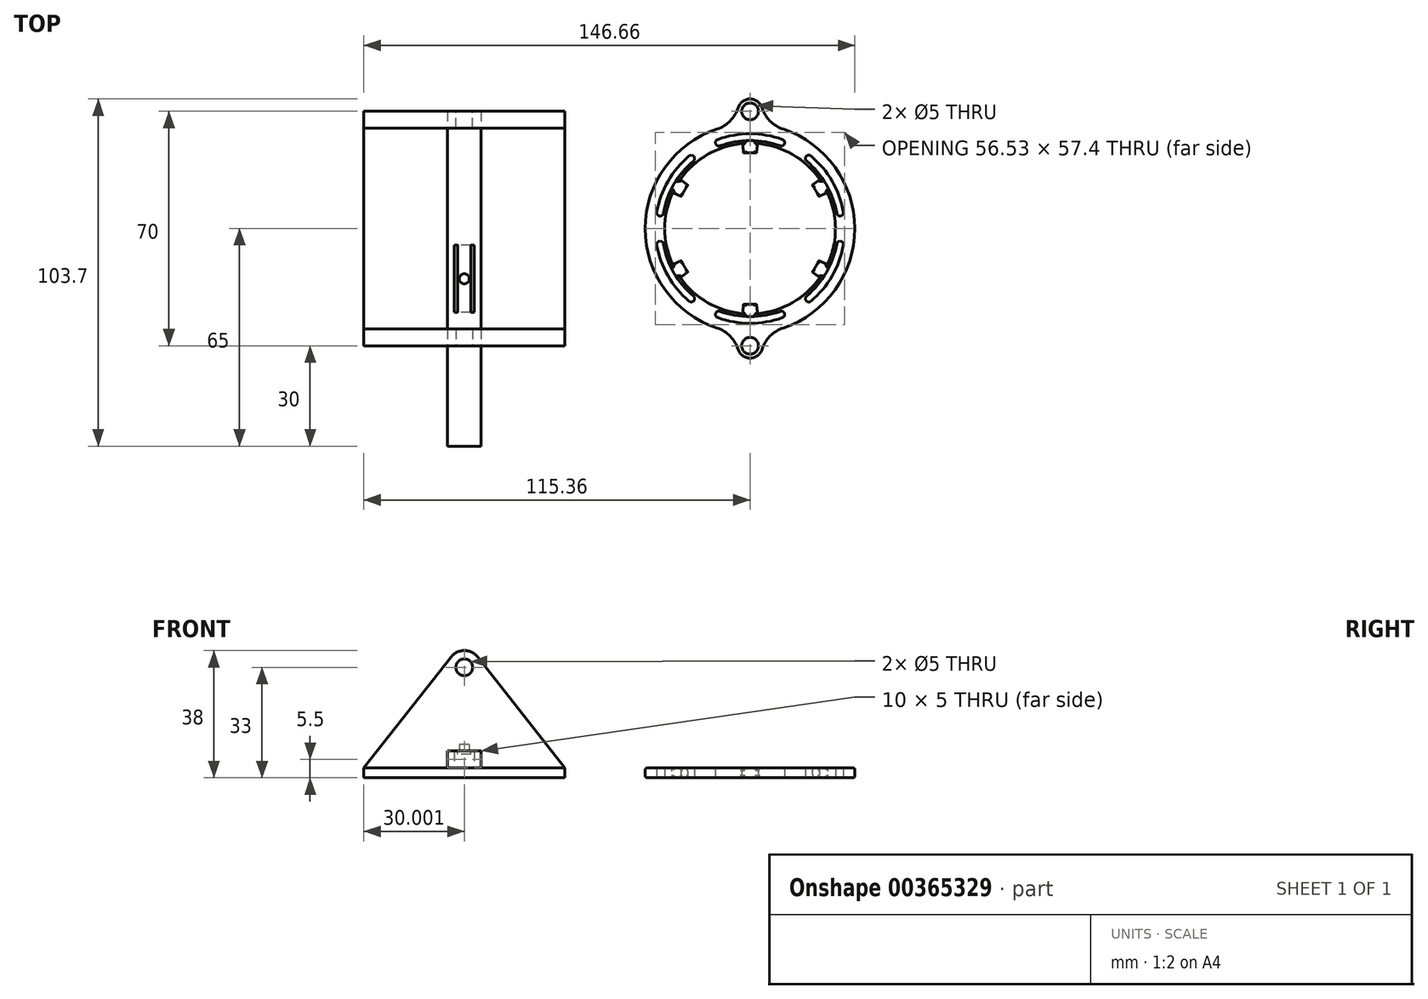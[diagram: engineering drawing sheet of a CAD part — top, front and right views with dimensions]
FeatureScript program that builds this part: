
annotation { "Feature Type Name" : "Feature", "Feature Type Description" : "" }
export const myFeature = defineFeature(function(context is Context, id is Id, definition is map)
    precondition{}
    {
        {
            var Q0;
            Q0=qCreatedBy(makeId("Top.planeOp"),FACE);
            var sketch = newSketch(context, id + "F0", { "sketchPlane" : qUnion([Q0])});
            skArc(sketch, "E0", {"start": v(-2.22, 25.4) * mm, "mid": v(-12.75, 22.08) * mm, "end": v(-20.89, 14.63) * mm});
            skArc(sketch, "E1", {"start": v(-9.89, 29.7) * mm, "mid": v(-31.3, 0) * mm, "end": v(-9.89, -29.7) * mm});
            skArc(sketch, "E2", {"start": v(1.97, 22.56) * mm, "mid": v(0, 22.65) * mm, "end": v(-1.97, 22.56) * mm});
            skArc(sketch, "E3", {"start": v(9, 24.71) * mm, "mid": v(0, 26.3) * mm, "end": v(-9, 24.71) * mm});
            skArc(sketch, "E4", {"start": v(9.68, 26.6) * mm, "mid": v(0, 28.3) * mm, "end": v(-9.68, 26.6) * mm});
            skLineSegment(sketch, "E5", {"start": v(0, 0) * mm, "end": v(-1.97, 22.56) * mm, "construction": true});
            skLineSegment(sketch, "E6", {"start": v(-1.97, 22.56) * mm, "end": v(-2.22, 25.4) * mm});
            skArc(sketch, "E7", {"start": v(-9.68, 26.6) * mm, "mid": v(-10.28, 25.31) * mm, "end": v(-9, 24.71) * mm});
            skLineSegment(sketch, "E8.MirrorCS", {"start": v(1.97, 22.56) * mm, "end": v(2.22, 25.4) * mm});
            skArc(sketch, "E9.MirrorCS", {"start": v(9.68, 26.6) * mm, "mid": v(10.28, 25.31) * mm, "end": v(9, 24.71) * mm});
            skLineSegment(sketch, "E10", {"start": v(-9.34, 25.65) * mm, "end": v(0, 0) * mm, "construction": true});
            skLineSegment(sketch, "E11", {"start": v(0, 0) * mm, "end": v(9.34, 25.65) * mm, "construction": true});
            skLineSegment(sketch, "E12", {"start": v(1.97, 22.56) * mm, "end": v(0, 0) * mm, "construction": true});
            skLineSegment(sketch, "E13.1.0", {"start": v(-20.53, 9.57) * mm, "end": v(-23.11, 10.78) * mm});
            skArc(sketch, "E13.1.1", {"start": v(-18.55, 13) * mm, "mid": v(-19.62, 11.33) * mm, "end": v(-20.53, 9.57) * mm});
            skLineSegment(sketch, "E13.1.2", {"start": v(-18.55, 13) * mm, "end": v(-20.89, 14.63) * mm});
            skArc(sketch, "E13.1.3", {"start": v(-16.9, 20.15) * mm, "mid": v(-22.78, 13.15) * mm, "end": v(-25.9, 4.57) * mm});
            skArc(sketch, "E13.1.4", {"start": v(-27.87, 4.91) * mm, "mid": v(-27.06, 3.76) * mm, "end": v(-25.9, 4.57) * mm});
            skArc(sketch, "E13.1.5", {"start": v(-18.2, 21.68) * mm, "mid": v(-24.5, 14.15) * mm, "end": v(-27.87, 4.91) * mm});
            skArc(sketch, "E13.1.6", {"start": v(-18.2, 21.68) * mm, "mid": v(-16.78, 21.56) * mm, "end": v(-16.9, 20.15) * mm});
            skLineSegment(sketch, "E13.2.0", {"start": v(-18.55, -13) * mm, "end": v(-20.89, -14.63) * mm});
            skArc(sketch, "E13.2.1", {"start": v(-20.53, -9.57) * mm, "mid": v(-19.62, -11.32) * mm, "end": v(-18.55, -13) * mm});
            skLineSegment(sketch, "E13.2.2", {"start": v(-20.53, -9.57) * mm, "end": v(-23.11, -10.78) * mm});
            skArc(sketch, "E13.2.3", {"start": v(-25.9, -4.57) * mm, "mid": v(-22.78, -13.15) * mm, "end": v(-16.9, -20.15) * mm});
            skArc(sketch, "E13.2.4", {"start": v(-18.2, -21.68) * mm, "mid": v(-16.78, -21.56) * mm, "end": v(-16.9, -20.15) * mm});
            skArc(sketch, "E13.2.5", {"start": v(-27.87, -4.91) * mm, "mid": v(-24.5, -14.15) * mm, "end": v(-18.2, -21.68) * mm});
            skArc(sketch, "E13.2.6", {"start": v(-27.87, -4.91) * mm, "mid": v(-27.06, -3.76) * mm, "end": v(-25.9, -4.57) * mm});
            skLineSegment(sketch, "E13.3.0", {"start": v(1.97, -22.56) * mm, "end": v(2.22, -25.4) * mm});
            skArc(sketch, "E13.3.1", {"start": v(-1.97, -22.56) * mm, "mid": v(0, -22.65) * mm, "end": v(1.97, -22.56) * mm});
            skLineSegment(sketch, "E13.3.2", {"start": v(-1.97, -22.56) * mm, "end": v(-2.22, -25.4) * mm});
            skArc(sketch, "E13.3.3", {"start": v(-9, -24.71) * mm, "mid": v(0, -26.3) * mm, "end": v(9, -24.71) * mm});
            skArc(sketch, "E13.3.4", {"start": v(9.68, -26.6) * mm, "mid": v(10.28, -25.31) * mm, "end": v(9, -24.71) * mm});
            skArc(sketch, "E13.3.5", {"start": v(-9.68, -26.6) * mm, "mid": v(0, -28.3) * mm, "end": v(9.68, -26.6) * mm});
            skArc(sketch, "E13.3.6", {"start": v(-9.68, -26.6) * mm, "mid": v(-10.28, -25.31) * mm, "end": v(-9, -24.71) * mm});
            skLineSegment(sketch, "E13.4.0", {"start": v(20.53, -9.57) * mm, "end": v(23.11, -10.78) * mm});
            skArc(sketch, "E13.4.1", {"start": v(18.55, -13) * mm, "mid": v(19.62, -11.33) * mm, "end": v(20.53, -9.57) * mm});
            skLineSegment(sketch, "E13.4.2", {"start": v(18.55, -13) * mm, "end": v(20.89, -14.63) * mm});
            skArc(sketch, "E13.4.3", {"start": v(16.9, -20.15) * mm, "mid": v(22.78, -13.15) * mm, "end": v(25.9, -4.57) * mm});
            skArc(sketch, "E13.4.4", {"start": v(27.87, -4.91) * mm, "mid": v(27.06, -3.76) * mm, "end": v(25.9, -4.57) * mm});
            skArc(sketch, "E13.4.5", {"start": v(18.2, -21.68) * mm, "mid": v(24.5, -14.15) * mm, "end": v(27.87, -4.91) * mm});
            skArc(sketch, "E13.4.6", {"start": v(18.2, -21.68) * mm, "mid": v(16.78, -21.56) * mm, "end": v(16.9, -20.15) * mm});
            skLineSegment(sketch, "E13.5.0", {"start": v(18.55, 13) * mm, "end": v(20.89, 14.63) * mm});
            skArc(sketch, "E13.5.1", {"start": v(20.53, 9.57) * mm, "mid": v(19.62, 11.33) * mm, "end": v(18.55, 13) * mm});
            skLineSegment(sketch, "E13.5.2", {"start": v(20.53, 9.57) * mm, "end": v(23.11, 10.78) * mm});
            skArc(sketch, "E13.5.3", {"start": v(25.9, 4.57) * mm, "mid": v(22.78, 13.15) * mm, "end": v(16.9, 20.15) * mm});
            skArc(sketch, "E13.5.4", {"start": v(18.2, 21.68) * mm, "mid": v(16.78, 21.56) * mm, "end": v(16.9, 20.15) * mm});
            skArc(sketch, "E13.5.5", {"start": v(27.87, 4.91) * mm, "mid": v(24.5, 14.15) * mm, "end": v(18.2, 21.68) * mm});
            skArc(sketch, "E13.5.6", {"start": v(27.87, 4.91) * mm, "mid": v(27.06, 3.76) * mm, "end": v(25.9, 4.57) * mm});
            skArc(sketch, "E14.trimOffspring", {"start": v(20.89, 14.63) * mm, "mid": v(12.75, 22.08) * mm, "end": v(2.22, 25.4) * mm});
            skArc(sketch, "E15.trimOffspring", {"start": v(-23.11, 10.78) * mm, "mid": v(-25.5, 0) * mm, "end": v(-23.11, -10.78) * mm});
            skArc(sketch, "E16.trimOffspring", {"start": v(-20.89, -14.63) * mm, "mid": v(-12.75, -22.08) * mm, "end": v(-2.22, -25.4) * mm});
            skArc(sketch, "E17.trimOffspring", {"start": v(23.11, -10.78) * mm, "mid": v(25.5, 0) * mm, "end": v(23.11, 10.78) * mm});
            skArc(sketch, "E18.trimOffspring", {"start": v(2.22, -25.4) * mm, "mid": v(12.75, -22.08) * mm, "end": v(20.89, -14.63) * mm});
            skArc(sketch, "E19", {"start": v(3.52, 36.13) * mm, "mid": v(0, 38.7) * mm, "end": v(-3.52, 36.13) * mm});
            skCircle(sketch, "E20", {"center": v(0, 35) * mm, "radius": 2.5 * mm});
            skArc(sketch, "E21", {"start": v(-9.89, 29.7) * mm, "mid": v(-5.94, 32.15) * mm, "end": v(-3.52, 36.13) * mm});
            skArc(sketch, "E22.MirrorCS", {"start": v(9.89, 29.7) * mm, "mid": v(5.94, 32.15) * mm, "end": v(3.52, 36.13) * mm});
            skArc(sketch, "E23.MirrorCS", {"start": v(-9.89, -29.7) * mm, "mid": v(-5.94, -32.15) * mm, "end": v(-3.52, -36.13) * mm});
            skArc(sketch, "E24.MirrorCS", {"start": v(3.52, -36.13) * mm, "mid": v(0, -38.7) * mm, "end": v(-3.52, -36.13) * mm});
            skArc(sketch, "E25.MirrorCS", {"start": v(9.89, -29.7) * mm, "mid": v(5.94, -32.15) * mm, "end": v(3.52, -36.13) * mm});
            skCircle(sketch, "E26.MirrorC", {"center": v(0, -35) * mm, "radius": 2.5 * mm});
            skArc(sketch, "E27.trimOffspring", {"start": v(9.89, -29.7) * mm, "mid": v(31.3, 0) * mm, "end": v(9.89, 29.7) * mm});
            skSolve(sketch);
        }
        {
            var Q0;
            Q0=makeQuery(id+"F0.imprint","IMPRINT",FACE,{"disambiguationData":[TD([[makeQuery(id+"F0.imprint","IMPRINT",EDGE,{"derivedFrom":sQuery(id+"F0.wireOp",EDGE,"E0")}),-1.0]])]});
            extrude(context, id + "F1", {"entities" : qUnion([Q0]), "depth" : 1.5 * mm});
        }
        {
            var Q0;
            Q0=makeQuery(id+"F1.opExtrude","CAP_EDGE",EDGE,{"disambiguationData":[OSD([sQuery(id+"F0.wireOp",EDGE,"E6")])],"isStart":true});
            var Q1;
            Q1=makeQuery(id+"F1.opExtrude","CAP_EDGE",EDGE,{"disambiguationData":[OSD([sQuery(id+"F0.wireOp",EDGE,"E8.MirrorCS")])],"isStart":true});
            var Q2;
            Q2=makeQuery(id+"F1.opExtrude","CAP_EDGE",EDGE,{"disambiguationData":[OSD([sQuery(id+"F0.wireOp",EDGE,"E13.5.0")])],"isStart":true});
            var Q3;
            Q3=makeQuery(id+"F1.opExtrude","CAP_EDGE",EDGE,{"disambiguationData":[OSD([sQuery(id+"F0.wireOp",EDGE,"E13.5.2")])],"isStart":true});
            var Q4;
            Q4=makeQuery(id+"F1.opExtrude","CAP_EDGE",EDGE,{"disambiguationData":[OSD([sQuery(id+"F0.wireOp",EDGE,"E13.4.2")])],"isStart":true});
            var Q5;
            Q5=makeQuery(id+"F1.opExtrude","CAP_EDGE",EDGE,{"disambiguationData":[OSD([sQuery(id+"F0.wireOp",EDGE,"E13.3.2")])],"isStart":true});
            var Q6;
            Q6=makeQuery(id+"F1.opExtrude","CAP_EDGE",EDGE,{"disambiguationData":[OSD([sQuery(id+"F0.wireOp",EDGE,"E13.4.0")])],"isStart":true});
            var Q7;
            Q7=makeQuery(id+"F1.opExtrude","CAP_EDGE",EDGE,{"disambiguationData":[OSD([sQuery(id+"F0.wireOp",EDGE,"E13.1.2")])],"isStart":true});
            var Q8;
            Q8=makeQuery(id+"F1.opExtrude","CAP_EDGE",EDGE,{"disambiguationData":[OSD([sQuery(id+"F0.wireOp",EDGE,"E13.2.2")])],"isStart":true});
            var Q9;
            Q9=makeQuery(id+"F1.opExtrude","CAP_EDGE",EDGE,{"disambiguationData":[OSD([sQuery(id+"F0.wireOp",EDGE,"E13.3.0")])],"isStart":true});
            var Q10;
            Q10=makeQuery(id+"F1.opExtrude","CAP_EDGE",EDGE,{"disambiguationData":[OSD([sQuery(id+"F0.wireOp",EDGE,"E13.2.0")])],"isStart":true});
            var Q11;
            Q11=makeQuery(id+"F1.opExtrude","CAP_EDGE",EDGE,{"disambiguationData":[OSD([sQuery(id+"F0.wireOp",EDGE,"E13.1.0")])],"isStart":true});
            fillet(context, id + "F2", {"entities" : qUnion([Q0, Q1, Q2, Q3, Q4, Q5, Q6, Q7, Q8, Q9, Q10, Q11]), "radius" : 1 * mm, "tangentPropagation" : true, "allowEdgeOverflow" : false});
        }
        {
            var Q0;
            Q0=makeQuery(id+"F1.opExtrude","CAP_EDGE",EDGE,{"disambiguationData":[OSD([sQuery(id+"F0.wireOp",EDGE,"E13.3.1")])],"isStart":true});
            var Q1;
            Q1=makeQuery(id+"F1.opExtrude","CAP_EDGE",EDGE,{"disambiguationData":[OSD([sQuery(id+"F0.wireOp",EDGE,"E13.4.1")])],"isStart":true});
            var Q2;
            Q2=makeQuery(id+"F1.opExtrude","CAP_EDGE",EDGE,{"disambiguationData":[OSD([sQuery(id+"F0.wireOp",EDGE,"E13.5.1")])],"isStart":true});
            var Q3;
            Q3=makeQuery(id+"F1.opExtrude","CAP_EDGE",EDGE,{"disambiguationData":[OSD([sQuery(id+"F0.wireOp",EDGE,"E2")])],"isStart":true});
            var Q4;
            Q4=makeQuery(id+"F1.opExtrude","CAP_EDGE",EDGE,{"disambiguationData":[OSD([sQuery(id+"F0.wireOp",EDGE,"E13.1.1")])],"isStart":true});
            var Q5;
            Q5=makeQuery(id+"F1.opExtrude","CAP_EDGE",EDGE,{"disambiguationData":[OSD([sQuery(id+"F0.wireOp",EDGE,"E13.2.1")])],"isStart":true});
            fillet(context, id + "F3", {"entities" : qUnion([Q0, Q1, Q2, Q3, Q4, Q5]), "radius" : 0.2 * mm, "tangentPropagation" : true, "allowEdgeOverflow" : false});
        }
        {
            var Q0;
            Q0=makeQuery(id+"F1.opExtrude","CAP_EDGE",EDGE,{"disambiguationData":[OSD([sQuery(id+"F0.wireOp",EDGE,"E14.trimOffspring")])],"isStart":true});
            var Q1;
            Q1=makeQuery(id+"F1.opExtrude","CAP_EDGE",EDGE,{"disambiguationData":[OSD([sQuery(id+"F0.wireOp",EDGE,"E0")])],"isStart":true});
            var Q2;
            Q2=makeQuery(id+"F1.opExtrude","CAP_EDGE",EDGE,{"disambiguationData":[OSD([sQuery(id+"F0.wireOp",EDGE,"E15.trimOffspring")])],"isStart":true});
            var Q3;
            Q3=makeQuery(id+"F1.opExtrude","CAP_EDGE",EDGE,{"disambiguationData":[OSD([sQuery(id+"F0.wireOp",EDGE,"E16.trimOffspring")])],"isStart":true});
            var Q4;
            Q4=makeQuery(id+"F1.opExtrude","CAP_EDGE",EDGE,{"disambiguationData":[OSD([sQuery(id+"F0.wireOp",EDGE,"E18.trimOffspring")])],"isStart":true});
            var Q5;
            Q5=makeQuery(id+"F1.opExtrude","CAP_EDGE",EDGE,{"disambiguationData":[OSD([sQuery(id+"F0.wireOp",EDGE,"E17.trimOffspring")])],"isStart":true});
            var Q6;
            Q6=makeQuery(id+"F1.opExtrude","CAP_EDGE",EDGE,{"disambiguationData":[OSD([sQuery(id+"F0.wireOp",EDGE,"E13.4.5")])],"isStart":true});
            var Q7;
            Q7=makeQuery(id+"F1.opExtrude","CAP_EDGE",EDGE,{"disambiguationData":[OSD([sQuery(id+"F0.wireOp",EDGE,"E13.3.3")])],"isStart":true});
            var Q8;
            Q8=makeQuery(id+"F1.opExtrude","CAP_EDGE",EDGE,{"disambiguationData":[OSD([sQuery(id+"F0.wireOp",EDGE,"E13.2.5")])],"isStart":true});
            var Q9;
            Q9=makeQuery(id+"F1.opExtrude","CAP_EDGE",EDGE,{"disambiguationData":[OSD([sQuery(id+"F0.wireOp",EDGE,"E13.1.5")])],"isStart":true});
            var Q10;
            Q10=makeQuery(id+"F1.opExtrude","CAP_EDGE",EDGE,{"disambiguationData":[OSD([sQuery(id+"F0.wireOp",EDGE,"E3")])],"isStart":true});
            var Q11;
            Q11=makeQuery(id+"F1.opExtrude","CAP_EDGE",EDGE,{"disambiguationData":[OSD([sQuery(id+"F0.wireOp",EDGE,"E13.5.3")])],"isStart":true});
            fillet(context, id + "F4", {"entities" : qUnion([Q0, Q1, Q2, Q3, Q4, Q5, Q6, Q7, Q8, Q9, Q10, Q11]), "radius" : 0.4 * mm, "tangentPropagation" : true, "allowEdgeOverflow" : false});
        }
        {
            var Q0;
            Q0=makeQuery(id+"F1.opExtrude","SWEPT_EDGE",EDGE,{"disambiguationData":[OSD([sQuery(id+"F0.wireOp",EDGE,"E13.5.0"),sQuery(id+"F0.wireOp",EDGE,"E14.trimOffspring")])]});
            var Q1;
            Q1=makeQuery(id+"F1.opExtrude","SWEPT_EDGE",EDGE,{"disambiguationData":[OSD([sQuery(id+"F0.wireOp",EDGE,"E13.4.0"),sQuery(id+"F0.wireOp",EDGE,"E17.trimOffspring")])]});
            var Q2;
            Q2=makeQuery(id+"F1.opExtrude","SWEPT_EDGE",EDGE,{"disambiguationData":[OSD([sQuery(id+"F0.wireOp",EDGE,"E13.4.2"),sQuery(id+"F0.wireOp",EDGE,"E18.trimOffspring")])]});
            var Q3;
            Q3=makeQuery(id+"F1.opExtrude","SWEPT_EDGE",EDGE,{"disambiguationData":[OSD([sQuery(id+"F0.wireOp",EDGE,"E13.3.2"),sQuery(id+"F0.wireOp",EDGE,"E16.trimOffspring")])]});
            var Q4;
            Q4=makeQuery(id+"F1.opExtrude","SWEPT_EDGE",EDGE,{"disambiguationData":[OSD([sQuery(id+"F0.wireOp",EDGE,"E13.2.2"),sQuery(id+"F0.wireOp",EDGE,"E15.trimOffspring")])]});
            var Q5;
            Q5=makeQuery(id+"F1.opExtrude","SWEPT_EDGE",EDGE,{"disambiguationData":[OSD([sQuery(id+"F0.wireOp",EDGE,"E13.3.0"),sQuery(id+"F0.wireOp",EDGE,"E18.trimOffspring")])]});
            var Q6;
            Q6=makeQuery(id+"F1.opExtrude","SWEPT_EDGE",EDGE,{"disambiguationData":[OSD([sQuery(id+"F0.wireOp",EDGE,"E13.2.0"),sQuery(id+"F0.wireOp",EDGE,"E16.trimOffspring")])]});
            var Q7;
            Q7=makeQuery(id+"F1.opExtrude","SWEPT_EDGE",EDGE,{"disambiguationData":[OSD([sQuery(id+"F0.wireOp",EDGE,"E0"),sQuery(id+"F0.wireOp",EDGE,"E13.1.2")])]});
            var Q8;
            Q8=makeQuery(id+"F1.opExtrude","SWEPT_EDGE",EDGE,{"disambiguationData":[OSD([sQuery(id+"F0.wireOp",EDGE,"E8.MirrorCS"),sQuery(id+"F0.wireOp",EDGE,"E14.trimOffspring")])]});
            var Q9;
            Q9=makeQuery(id+"F1.opExtrude","SWEPT_EDGE",EDGE,{"disambiguationData":[OSD([sQuery(id+"F0.wireOp",EDGE,"E13.1.0"),sQuery(id+"F0.wireOp",EDGE,"E15.trimOffspring")])]});
            var Q10;
            Q10=makeQuery(id+"F1.opExtrude","SWEPT_EDGE",EDGE,{"disambiguationData":[OSD([sQuery(id+"F0.wireOp",EDGE,"E0"),sQuery(id+"F0.wireOp",EDGE,"E6")])]});
            var Q11;
            Q11=makeQuery(id+"F1.opExtrude","SWEPT_EDGE",EDGE,{"disambiguationData":[OSD([sQuery(id+"F0.wireOp",EDGE,"E13.5.2"),sQuery(id+"F0.wireOp",EDGE,"E17.trimOffspring")])]});
            fillet(context, id + "F5", {"entities" : qUnion([Q0, Q1, Q2, Q3, Q4, Q5, Q6, Q7, Q8, Q9, Q10, Q11]), "radius" : 0.5 * mm, "tangentPropagation" : true, "allowEdgeOverflow" : false});
        }
        {
            var Q0;
            Q0=makeQuery(id+"F1.opExtrude","CAP_EDGE",EDGE,{"disambiguationData":[OSD([sQuery(id+"F0.wireOp",EDGE,"E27.trimOffspring")])],"isStart":true});
            var Q1;
            Q1=makeQuery(id+"F1.opExtrude","CAP_EDGE",EDGE,{"disambiguationData":[OSD([sQuery(id+"F0.wireOp",EDGE,"E26.MirrorC")])],"isStart":true});
            var Q2;
            Q2=makeQuery(id+"F1.opExtrude","CAP_EDGE",EDGE,{"disambiguationData":[OSD([sQuery(id+"F0.wireOp",EDGE,"E20")])],"isStart":true});
            fillet(context, id + "F6", {"entities" : qUnion([Q0, Q1, Q2]), "radius" : 0.6 * mm, "tangentPropagation" : true, "allowEdgeOverflow" : false});
        }
        {
            var Q0;
            Q0=makeQuery(id+"F1.opExtrude","SWEPT_BODY",BODY,{"disambiguationData":[OSD([sQuery(id+"F0.wireOp",EDGE,"E0"),sQuery(id+"F0.wireOp",EDGE,"E1"),sQuery(id+"F0.wireOp",EDGE,"E2"),sQuery(id+"F0.wireOp",EDGE,"E3"),sQuery(id+"F0.wireOp",EDGE,"E4"),sQuery(id+"F0.wireOp",EDGE,"E6"),sQuery(id+"F0.wireOp",EDGE,"E7"),sQuery(id+"F0.wireOp",EDGE,"E8.MirrorCS"),sQuery(id+"F0.wireOp",EDGE,"E9.MirrorCS"),sQuery(id+"F0.wireOp",EDGE,"E13.1.0"),sQuery(id+"F0.wireOp",EDGE,"E13.1.1"),sQuery(id+"F0.wireOp",EDGE,"E13.1.2"),sQuery(id+"F0.wireOp",EDGE,"E13.1.3"),sQuery(id+"F0.wireOp",EDGE,"E13.1.4"),sQuery(id+"F0.wireOp",EDGE,"E13.1.5"),sQuery(id+"F0.wireOp",EDGE,"E13.1.6"),sQuery(id+"F0.wireOp",EDGE,"E13.2.0"),sQuery(id+"F0.wireOp",EDGE,"E13.2.1"),sQuery(id+"F0.wireOp",EDGE,"E13.2.2"),sQuery(id+"F0.wireOp",EDGE,"E13.2.3"),sQuery(id+"F0.wireOp",EDGE,"E13.2.4"),sQuery(id+"F0.wireOp",EDGE,"E13.2.5"),sQuery(id+"F0.wireOp",EDGE,"E13.2.6"),sQuery(id+"F0.wireOp",EDGE,"E13.3.0"),sQuery(id+"F0.wireOp",EDGE,"E13.3.1"),sQuery(id+"F0.wireOp",EDGE,"E13.3.2"),sQuery(id+"F0.wireOp",EDGE,"E13.3.3"),sQuery(id+"F0.wireOp",EDGE,"E13.3.4"),sQuery(id+"F0.wireOp",EDGE,"E13.3.5"),sQuery(id+"F0.wireOp",EDGE,"E13.3.6"),sQuery(id+"F0.wireOp",EDGE,"E13.4.0"),sQuery(id+"F0.wireOp",EDGE,"E13.4.1"),sQuery(id+"F0.wireOp",EDGE,"E13.4.2"),sQuery(id+"F0.wireOp",EDGE,"E13.4.3"),sQuery(id+"F0.wireOp",EDGE,"E13.4.4"),sQuery(id+"F0.wireOp",EDGE,"E13.4.5"),sQuery(id+"F0.wireOp",EDGE,"E13.4.6"),sQuery(id+"F0.wireOp",EDGE,"E13.5.0"),sQuery(id+"F0.wireOp",EDGE,"E13.5.1"),sQuery(id+"F0.wireOp",EDGE,"E13.5.2"),sQuery(id+"F0.wireOp",EDGE,"E13.5.3"),sQuery(id+"F0.wireOp",EDGE,"E13.5.4"),sQuery(id+"F0.wireOp",EDGE,"E13.5.5"),sQuery(id+"F0.wireOp",EDGE,"E13.5.6"),sQuery(id+"F0.wireOp",EDGE,"E14.trimOffspring"),sQuery(id+"F0.wireOp",EDGE,"E15.trimOffspring"),sQuery(id+"F0.wireOp",EDGE,"E16.trimOffspring"),sQuery(id+"F0.wireOp",EDGE,"E17.trimOffspring"),sQuery(id+"F0.wireOp",EDGE,"E18.trimOffspring"),sQuery(id+"F0.wireOp",EDGE,"E19"),sQuery(id+"F0.wireOp",EDGE,"E20"),sQuery(id+"F0.wireOp",EDGE,"E21"),sQuery(id+"F0.wireOp",EDGE,"E22.MirrorCS"),sQuery(id+"F0.wireOp",EDGE,"E23.MirrorCS"),sQuery(id+"F0.wireOp",EDGE,"E24.MirrorCS"),sQuery(id+"F0.wireOp",EDGE,"E25.MirrorCS"),sQuery(id+"F0.wireOp",EDGE,"E26.MirrorC"),sQuery(id+"F0.wireOp",EDGE,"E27.trimOffspring")])]});
            var Q1;
            Q1=makeQuery(id+"F1.opExtrude","CAP_FACE",FACE,{"disambiguationData":[OSD([sQuery(id+"F0.wireOp",EDGE,"E0"),sQuery(id+"F0.wireOp",EDGE,"E1"),sQuery(id+"F0.wireOp",EDGE,"E2"),sQuery(id+"F0.wireOp",EDGE,"E3"),sQuery(id+"F0.wireOp",EDGE,"E4"),sQuery(id+"F0.wireOp",EDGE,"E6"),sQuery(id+"F0.wireOp",EDGE,"E7"),sQuery(id+"F0.wireOp",EDGE,"E8.MirrorCS"),sQuery(id+"F0.wireOp",EDGE,"E9.MirrorCS"),sQuery(id+"F0.wireOp",EDGE,"E13.1.0"),sQuery(id+"F0.wireOp",EDGE,"E13.1.1"),sQuery(id+"F0.wireOp",EDGE,"E13.1.2"),sQuery(id+"F0.wireOp",EDGE,"E13.1.3"),sQuery(id+"F0.wireOp",EDGE,"E13.1.4"),sQuery(id+"F0.wireOp",EDGE,"E13.1.5"),sQuery(id+"F0.wireOp",EDGE,"E13.1.6"),sQuery(id+"F0.wireOp",EDGE,"E13.2.0"),sQuery(id+"F0.wireOp",EDGE,"E13.2.1"),sQuery(id+"F0.wireOp",EDGE,"E13.2.2"),sQuery(id+"F0.wireOp",EDGE,"E13.2.3"),sQuery(id+"F0.wireOp",EDGE,"E13.2.4"),sQuery(id+"F0.wireOp",EDGE,"E13.2.5"),sQuery(id+"F0.wireOp",EDGE,"E13.2.6"),sQuery(id+"F0.wireOp",EDGE,"E13.3.0"),sQuery(id+"F0.wireOp",EDGE,"E13.3.1"),sQuery(id+"F0.wireOp",EDGE,"E13.3.2"),sQuery(id+"F0.wireOp",EDGE,"E13.3.3"),sQuery(id+"F0.wireOp",EDGE,"E13.3.4"),sQuery(id+"F0.wireOp",EDGE,"E13.3.5"),sQuery(id+"F0.wireOp",EDGE,"E13.3.6"),sQuery(id+"F0.wireOp",EDGE,"E13.4.0"),sQuery(id+"F0.wireOp",EDGE,"E13.4.1"),sQuery(id+"F0.wireOp",EDGE,"E13.4.2"),sQuery(id+"F0.wireOp",EDGE,"E13.4.3"),sQuery(id+"F0.wireOp",EDGE,"E13.4.4"),sQuery(id+"F0.wireOp",EDGE,"E13.4.5"),sQuery(id+"F0.wireOp",EDGE,"E13.4.6"),sQuery(id+"F0.wireOp",EDGE,"E13.5.0"),sQuery(id+"F0.wireOp",EDGE,"E13.5.1"),sQuery(id+"F0.wireOp",EDGE,"E13.5.2"),sQuery(id+"F0.wireOp",EDGE,"E13.5.3"),sQuery(id+"F0.wireOp",EDGE,"E13.5.4"),sQuery(id+"F0.wireOp",EDGE,"E13.5.5"),sQuery(id+"F0.wireOp",EDGE,"E13.5.6"),sQuery(id+"F0.wireOp",EDGE,"E14.trimOffspring"),sQuery(id+"F0.wireOp",EDGE,"E15.trimOffspring"),sQuery(id+"F0.wireOp",EDGE,"E16.trimOffspring"),sQuery(id+"F0.wireOp",EDGE,"E17.trimOffspring"),sQuery(id+"F0.wireOp",EDGE,"E18.trimOffspring"),sQuery(id+"F0.wireOp",EDGE,"E19"),sQuery(id+"F0.wireOp",EDGE,"E20"),sQuery(id+"F0.wireOp",EDGE,"E21"),sQuery(id+"F0.wireOp",EDGE,"E22.MirrorCS"),sQuery(id+"F0.wireOp",EDGE,"E23.MirrorCS"),sQuery(id+"F0.wireOp",EDGE,"E24.MirrorCS"),sQuery(id+"F0.wireOp",EDGE,"E25.MirrorCS"),sQuery(id+"F0.wireOp",EDGE,"E26.MirrorC"),sQuery(id+"F0.wireOp",EDGE,"E27.trimOffspring")])],"isStart":false});
            mirror(context, id + "F7", {"operationType" : NewBodyOperationType.ADD, "entities" : qUnion([Q0]), "mirrorPlane" : qUnion([Q1])});
        }
        {
            var Q0;
            Q0=qCreatedBy(makeId("Top.planeOp"),FACE);
            var sketch = newSketch(context, id + "F8", { "sketchPlane" : qUnion([Q0])});
            skLineSegment(sketch, "E28.bottom", {"start": v(-115.36, 35) * mm, "end": v(-55.36, 35) * mm});
            skLineSegment(sketch, "E28.top", {"start": v(-115.36, -35) * mm, "end": v(-55.36, -35) * mm});
            skLineSegment(sketch, "E28.left", {"start": v(-115.36, 35) * mm, "end": v(-115.36, -35) * mm});
            skLineSegment(sketch, "E28.right", {"start": v(-55.36, 35) * mm, "end": v(-55.36, -35) * mm});
            skSolve(sketch);
        }
        {
            var Q0;
            Q0=makeQuery(id+"F8.imprint","IMPRINT",FACE,{"disambiguationData":[TD([[makeQuery(id+"F8.imprint","IMPRINT",EDGE,{"derivedFrom":sQuery(id+"F8.wireOp",EDGE,"E28.bottom")}),-1.0]])]});
            extrude(context, id + "F9", {"entities" : qUnion([Q0]), "depth" : 3 * mm});
        }
        {
            var Q0;
            Q0=makeQuery(id+"F9.opExtrude","SWEPT_FACE",FACE,{"disambiguationData":[OSD([sQuery(id+"F8.wireOp",EDGE,"E28.top")])]});
            var sketch = newSketch(context, id + "F10", { "sketchPlane" : qUnion([Q0])});
            skCircle(sketch, "E29", {"center": v(-85.36, 33) * mm, "radius": 2.5 * mm});
            skArc(sketch, "E30", {"start": v(-81.43, 36.1) * mm, "mid": v(-85.36, 38) * mm, "end": v(-89.29, 36.1) * mm});
            skLineSegment(sketch, "E31", {"start": v(-81.43, 36.1) * mm, "end": v(-55.36, 3) * mm});
            skLineSegment(sketch, "E32", {"start": v(-55.36, 3) * mm, "end": v(-115.36, 3) * mm});
            skLineSegment(sketch, "E33", {"start": v(-115.36, 3) * mm, "end": v(-89.29, 36.1) * mm});
            skLineSegment(sketch, "E34.bottom", {"start": v(-90.36, 3) * mm, "end": v(-80.36, 3) * mm});
            skLineSegment(sketch, "E34.top", {"start": v(-90.36, 8) * mm, "end": v(-80.36, 8) * mm});
            skLineSegment(sketch, "E34.left", {"start": v(-90.36, 3) * mm, "end": v(-90.36, 8) * mm});
            skLineSegment(sketch, "E34.right", {"start": v(-80.36, 3) * mm, "end": v(-80.36, 8) * mm});
            skPoint(sketch, "E35", {"position": v(-85.36, 8) * mm});
            skSolve(sketch);
        }
        {
            var Q0;
            Q0=makeQuery(id+"F10.imprint","IMPRINT",FACE,{"disambiguationData":[TD([[makeQuery(id+"F10.imprint","IMPRINT",EDGE,{"derivedFrom":sQuery(id+"F10.wireOp",EDGE,"E29")}),-1.0]])]});
            extrude(context, id + "F11", {"entities" : qUnion([Q0]), "operationType" : NewBodyOperationType.ADD, "oppositeDirection" : true, "depth" : 5 * mm});
        }
        {
            var Q0;
            Q0=makeQuery(id+"F9.opExtrude","SWEPT_BODY",BODY,{"disambiguationData":[OSD([sQuery(id+"F8.wireOp",EDGE,"E28.bottom"),sQuery(id+"F8.wireOp",EDGE,"E28.top"),sQuery(id+"F8.wireOp",EDGE,"E28.left"),sQuery(id+"F8.wireOp",EDGE,"E28.right")])]});
            var Q1;
            Q1=qCreatedBy(makeId("Front.planeOp"),FACE);
            mirror(context, id + "F12", {"operationType" : NewBodyOperationType.ADD, "entities" : qUnion([Q0]), "mirrorPlane" : qUnion([Q1])});
        }
        {
            var Q0;
            Q0=makeQuery(id+"F9.opExtrude","CAP_FACE",FACE,{"disambiguationData":[OSD([sQuery(id+"F8.wireOp",EDGE,"E28.bottom"),sQuery(id+"F8.wireOp",EDGE,"E28.top"),sQuery(id+"F8.wireOp",EDGE,"E28.left"),sQuery(id+"F8.wireOp",EDGE,"E28.right")])],"isStart":false});
            var sketch = newSketch(context, id + "F13", { "sketchPlane" : qUnion([Q0])});
            skLineSegment(sketch, "E36.bottom", {"start": v(-80.36, 35) * mm, "end": v(-90.36, 35) * mm});
            skLineSegment(sketch, "E36.top", {"start": v(-80.36, -65) * mm, "end": v(-90.36, -65) * mm});
            skLineSegment(sketch, "E36.left", {"start": v(-80.36, 35) * mm, "end": v(-80.36, -65) * mm});
            skLineSegment(sketch, "E36.right", {"start": v(-90.36, 35) * mm, "end": v(-90.36, -65) * mm});
            skLineSegment(sketch, "E37.bottom", {"start": v(-82.36, -5) * mm, "end": v(-88.36, -5) * mm});
            skLineSegment(sketch, "E37.top", {"start": v(-82.36, -25) * mm, "end": v(-88.36, -25) * mm});
            skLineSegment(sketch, "E37.left", {"start": v(-82.36, -5) * mm, "end": v(-82.36, -25) * mm});
            skLineSegment(sketch, "E37.right", {"start": v(-88.36, -5) * mm, "end": v(-88.36, -25) * mm});
            skSolve(sketch);
        }
        {
            var Q0;
            Q0 = qSketchRegion(id + "F13", true);
            extrude(context, id + "F14", {"entities" : qUnion([Q0]), "depth" : 5 * mm});
        }
        {
            var Q0;
            Q0=makeQuery(id+"F14.opExtrude","CAP_FACE",FACE,{"disambiguationData":[OSD([sQuery(id+"F13.wireOp",EDGE,"E36.bottom"),sQuery(id+"F13.wireOp",EDGE,"E36.top"),sQuery(id+"F13.wireOp",EDGE,"E36.left"),sQuery(id+"F13.wireOp",EDGE,"E36.right"),sQuery(id+"F13.wireOp",EDGE,"E37.bottom"),sQuery(id+"F13.wireOp",EDGE,"E37.top"),sQuery(id+"F13.wireOp",EDGE,"E37.left"),sQuery(id+"F13.wireOp",EDGE,"E37.right")])],"isStart":false});
            var sketch = newSketch(context, id + "F15", { "sketchPlane" : qUnion([Q0])});
            skLineSegment(sketch, "E38.bottom", {"start": v(-87.36, -5) * mm, "end": v(-83.36, -5) * mm});
            skLineSegment(sketch, "E38.top", {"start": v(-87.36, -25) * mm, "end": v(-83.36, -25) * mm});
            skLineSegment(sketch, "E38.left", {"start": v(-87.36, -5) * mm, "end": v(-87.36, -25) * mm});
            skLineSegment(sketch, "E38.right", {"start": v(-83.36, -5) * mm, "end": v(-83.36, -25) * mm});
            skCircle(sketch, "E39", {"center": v(-85.36, -15) * mm, "radius": 1.5 * mm});
            skPoint(sketch, "E39.centerSnap0", {"position": v(-85.36, -25) * mm});
            skPoint(sketch, "E39.centerSnap1", {"position": v(-83.36, -15) * mm});
            skSolve(sketch);
        }
        {
            var Q0;
            Q0=makeQuery(id+"F15.imprint","IMPRINT",FACE,{"disambiguationData":[TD([[makeQuery(id+"F15.imprint","IMPRINT",EDGE,{"derivedFrom":sQuery(id+"F15.wireOp",EDGE,"E39")}),1.0]])]});
            extrude(context, id + "F16", {"entities" : qUnion([Q0]), "depth" : 2 * mm});
        }
        {
            var Q0;
            Q0=makeQuery(id+"F15.imprint","IMPRINT",FACE,{"disambiguationData":[TD([[makeQuery(id+"F15.imprint","IMPRINT",EDGE,{"derivedFrom":sQuery(id+"F15.wireOp",EDGE,"E38.bottom")}),1.0]])]});
            var Q1;
            Q1=makeQuery(id+"F15.imprint","IMPRINT",FACE,{"disambiguationData":[TD([[makeQuery(id+"F15.imprint","IMPRINT",EDGE,{"derivedFrom":sQuery(id+"F15.wireOp",EDGE,"E39")}),1.0]])]});
            extrude(context, id + "F17", {"entities" : qUnion([Q0, Q1]), "operationType" : NewBodyOperationType.ADD, "oppositeDirection" : true, "depth" : 1 * mm});
        }
    });
